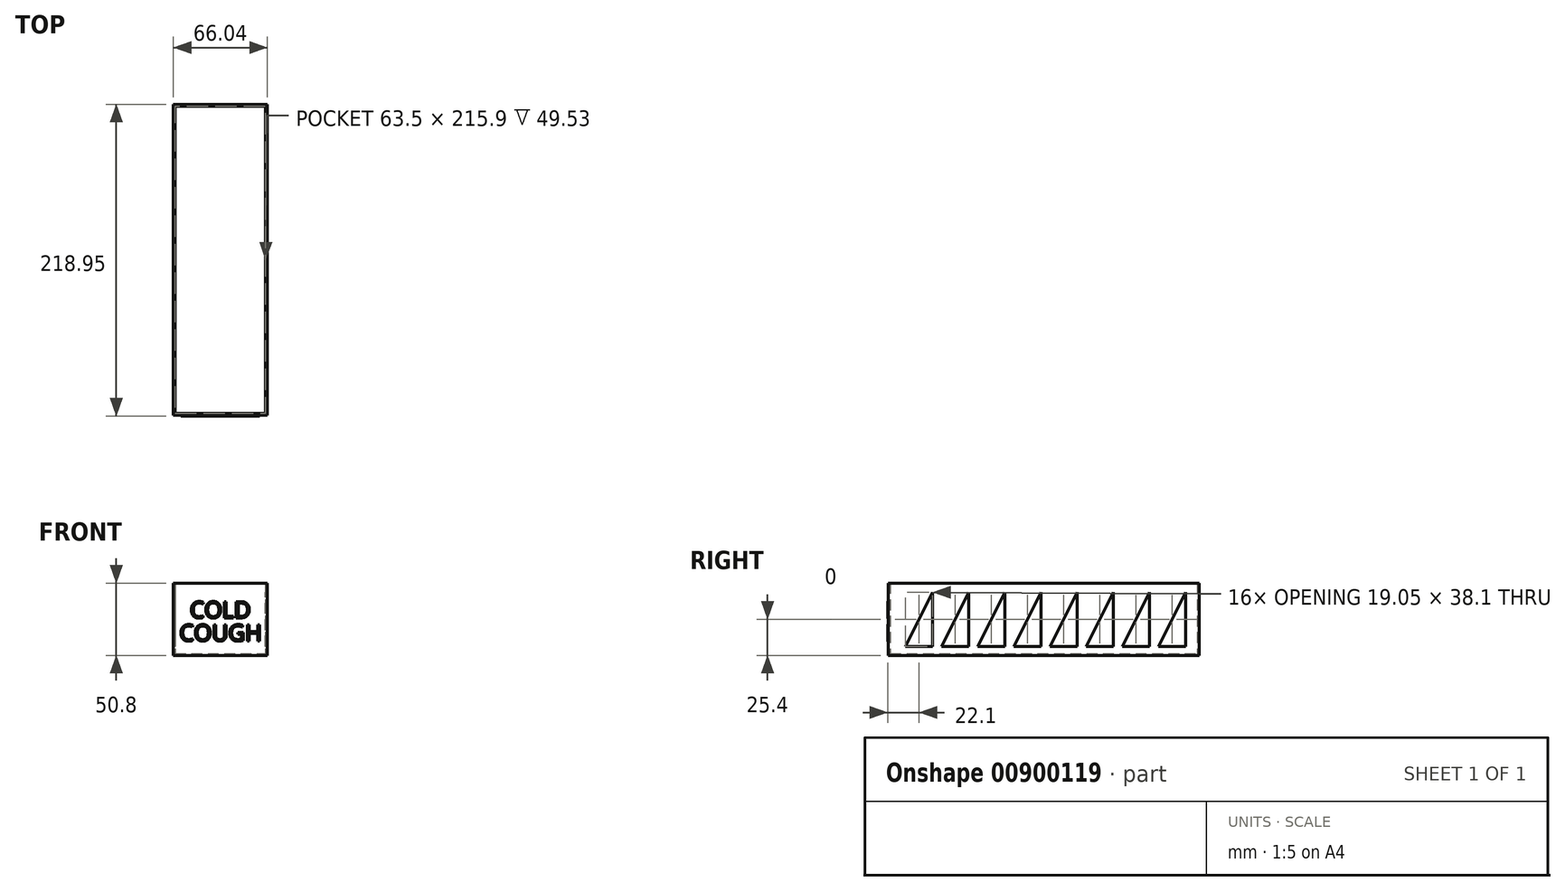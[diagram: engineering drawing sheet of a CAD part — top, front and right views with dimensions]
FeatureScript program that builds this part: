
annotation { "Feature Type Name" : "Feature", "Feature Type Description" : "" }
export const myFeature = defineFeature(function(context is Context, id is Id, definition is map)
    precondition{}
    {
        {
            var Q0;
            Q0=qCreatedBy(makeId("Top.planeOp"),FACE);
            var sketch = newSketch(context, id + "F0", { "sketchPlane" : qUnion([Q0])});
            skLineSegment(sketch, "E0.bottom", {"start": v(31.75, 107.95) * mm, "end": v(-31.75, 107.95) * mm});
            skLineSegment(sketch, "E0.top", {"start": v(31.75, -107.95) * mm, "end": v(-31.75, -107.95) * mm});
            skLineSegment(sketch, "E0.left", {"start": v(31.75, 107.95) * mm, "end": v(31.75, -107.95) * mm});
            skLineSegment(sketch, "E0.right", {"start": v(-31.75, 107.95) * mm, "end": v(-31.75, -107.95) * mm});
            skPoint(sketch, "E0.middle", {"position": v(0, 0) * mm});
            skLineSegment(sketch, "E1.0", {"start": v(33.02, 109.22) * mm, "end": v(-33.02, 109.22) * mm});
            skLineSegment(sketch, "E1.1", {"start": v(33.02, 109.22) * mm, "end": v(33.02, -109.22) * mm});
            skLineSegment(sketch, "E1.2", {"start": v(33.02, -109.22) * mm, "end": v(-33.02, -109.22) * mm});
            skLineSegment(sketch, "E1.3", {"start": v(-33.02, 109.22) * mm, "end": v(-33.02, -109.22) * mm});
            skSolve(sketch);
        }
        {
            var Q0;
            Q0=qSketchRegion(id+"F0",true);
            var Q1;
            Q1=makeQuery(id+"F0.imprint","IMPRINT",FACE,{"disambiguationData":[TD([[makeQuery(id+"F0.imprint","IMPRINT",EDGE,{"derivedFrom":sQuery(id+"F0.wireOp",EDGE,"E0.bottom")}),1.0]])]});
            extrude(context, id + "F1", {"entities" : qUnion([Q0, Q1]), "depth" : 1.27 * mm, "offsetDistance" : 25.4 * mm});
        }
        {
            var Q0;
            Q0=qSketchRegion(id+"F0",true);
            extrude(context, id + "F2", {"entities" : qUnion([Q0]), "operationType" : NewBodyOperationType.ADD, "depth" : 50.8 * mm, "offsetDistance" : 25.4 * mm});
        }
        {
            var Q0;
            {var subQ0=sQuery(id+"F0.wireOp",EDGE,"E1.3");Q0=makeQuery(id+"F2.boolean.opBoolean","MERGE",FACE,{"derivedFrom":[makeQuery(id+"F1.opExtrude","SWEPT_FACE",FACE,{"disambiguationData":[OSD([subQ0])]}),makeQuery(id+"F2.opExtrude","SWEPT_FACE",FACE,{"disambiguationData":[OSD([subQ0])]})]});}
            var sketch = newSketch(context, id + "F3", { "sketchPlane" : qUnion([Q0])});
            skLineSegment(sketch, "E2", {"start": v(-99.7, 44.45) * mm, "end": v(-99.7, 6.35) * mm});
            skLineSegment(sketch, "E3", {"start": v(-99.7, 6.35) * mm, "end": v(-80.65, 6.35) * mm});
            skLineSegment(sketch, "E4", {"start": v(-80.64, 6.35) * mm, "end": v(-99.7, 44.45) * mm});
            skLineSegment(sketch, "E5.1.0.0", {"start": v(-55.25, 6.35) * mm, "end": v(-74.3, 44.45) * mm});
            skLineSegment(sketch, "E5.1.0.1", {"start": v(-74.3, 44.45) * mm, "end": v(-74.3, 6.35) * mm});
            skLineSegment(sketch, "E5.1.0.2", {"start": v(-74.3, 44.45) * mm, "end": v(-74.3, 44.45) * mm});
            skLineSegment(sketch, "E5.1.0.3", {"start": v(-74.3, 6.35) * mm, "end": v(-55.25, 6.35) * mm});
            skLineSegment(sketch, "E5.2.0.0", {"start": v(-29.85, 6.35) * mm, "end": v(-48.9, 44.45) * mm});
            skLineSegment(sketch, "E5.2.0.1", {"start": v(-48.9, 44.45) * mm, "end": v(-48.9, 6.35) * mm});
            skLineSegment(sketch, "E5.2.0.2", {"start": v(-48.9, 44.45) * mm, "end": v(-48.9, 44.45) * mm});
            skLineSegment(sketch, "E5.2.0.3", {"start": v(-48.9, 6.35) * mm, "end": v(-29.85, 6.35) * mm});
            skLineSegment(sketch, "E5.3.0.0", {"start": v(-4.45, 6.35) * mm, "end": v(-23.5, 44.45) * mm});
            skLineSegment(sketch, "E5.3.0.1", {"start": v(-23.5, 44.45) * mm, "end": v(-23.5, 6.35) * mm});
            skLineSegment(sketch, "E5.3.0.2", {"start": v(-23.5, 44.45) * mm, "end": v(-23.5, 44.45) * mm});
            skLineSegment(sketch, "E5.3.0.3", {"start": v(-23.5, 6.35) * mm, "end": v(-4.45, 6.35) * mm});
            skLineSegment(sketch, "E5.4.0.0", {"start": v(20.95, 6.35) * mm, "end": v(1.9, 44.45) * mm});
            skLineSegment(sketch, "E5.4.0.1", {"start": v(1.9, 44.45) * mm, "end": v(1.9, 6.35) * mm});
            skLineSegment(sketch, "E5.4.0.2", {"start": v(1.9, 44.45) * mm, "end": v(1.9, 44.45) * mm});
            skLineSegment(sketch, "E5.4.0.3", {"start": v(1.9, 6.35) * mm, "end": v(20.95, 6.35) * mm});
            skLineSegment(sketch, "E5.5.0.0", {"start": v(46.35, 6.35) * mm, "end": v(27.3, 44.45) * mm});
            skLineSegment(sketch, "E5.5.0.1", {"start": v(27.3, 44.45) * mm, "end": v(27.3, 6.35) * mm});
            skLineSegment(sketch, "E5.5.0.2", {"start": v(27.3, 44.45) * mm, "end": v(27.3, 44.45) * mm});
            skLineSegment(sketch, "E5.5.0.3", {"start": v(27.3, 6.35) * mm, "end": v(46.35, 6.35) * mm});
            skLineSegment(sketch, "E5.6.0.0", {"start": v(71.75, 6.35) * mm, "end": v(52.7, 44.45) * mm});
            skLineSegment(sketch, "E5.6.0.1", {"start": v(52.7, 44.45) * mm, "end": v(52.7, 6.35) * mm});
            skLineSegment(sketch, "E5.6.0.2", {"start": v(52.7, 44.45) * mm, "end": v(52.7, 44.45) * mm});
            skLineSegment(sketch, "E5.6.0.3", {"start": v(52.7, 6.35) * mm, "end": v(71.75, 6.35) * mm});
            skLineSegment(sketch, "E5.7.0.0", {"start": v(97.15, 6.35) * mm, "end": v(78.1, 44.45) * mm});
            skLineSegment(sketch, "E5.7.0.1", {"start": v(78.1, 44.45) * mm, "end": v(78.1, 6.35) * mm});
            skLineSegment(sketch, "E5.7.0.2", {"start": v(78.1, 44.45) * mm, "end": v(78.1, 44.45) * mm});
            skLineSegment(sketch, "E5.7.0.3", {"start": v(78.1, 6.35) * mm, "end": v(97.15, 6.35) * mm});
            skLineSegment(sketch, "E5.direction1", {"start": v(-80.65, 6.35) * mm, "end": v(-55.25, 6.35) * mm, "construction": true});
            skSolve(sketch);
        }
        {
            var Q0;
            Q0=qSketchRegion(id+"F3",true);
            extrude(context, id + "F4", {"entities" : qUnion([Q0]), "operationType" : NewBodyOperationType.REMOVE, "oppositeDirection" : true, "depth" : 76.2 * mm, "offsetDistance" : 25.4 * mm});
        }
        {
            var Q0;
            {var subQ0=sQuery(id+"F0.wireOp",EDGE,"E1.2");Q0=makeQuery(id+"F2.boolean.opBoolean","MERGE",FACE,{"derivedFrom":[makeQuery(id+"F1.opExtrude","SWEPT_FACE",FACE,{"disambiguationData":[OSD([subQ0])]}),makeQuery(id+"F2.opExtrude","SWEPT_FACE",FACE,{"disambiguationData":[OSD([subQ0])]})]});}
            var sketch = newSketch(context, id + "F5", { "sketchPlane" : qUnion([Q0])});
            skText(sketch, "E6", { "text": "COLD", "fontName": "OpenSans-Regular.ttf"});
            skText(sketch, "E7", { "text": "COUGH", "fontName": "OpenSans-Regular.ttf"});
            const initialGuessF5  = {"E6": [-0.02136, 0.02634, 1, 0, 0.01156], "E7": [-0.02873, 0.01014, 1, 0, 0.01156]};
            skSetInitialGuess(sketch, initialGuessF5);
            skSolve(sketch);
        }
        {
            var Q0;
            Q0=qSketchRegion(id+"F5",true);
            extrude(context, id + "F6", {"entities" : qUnion([Q0]), "operationType" : NewBodyOperationType.ADD, "depth" : 0.5 * mm, "offsetDistance" : 25.4 * mm});
        }
    });
